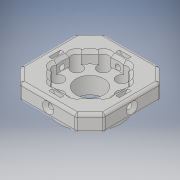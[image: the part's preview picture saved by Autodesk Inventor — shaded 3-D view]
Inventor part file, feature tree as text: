
AUTODESK INVENTOR PART (.ipt)
format: ipt  version: 2019 (Build 230136000, 136)  size: 383,488 bytes
history: native  units: in
note: dims shown in document units (in); Inventor stores cm internally (conversion verified against a paired STEP export)
features: extrude x9, sketch x6, plane x3, pattern_circular x3, chamfer x2, other x1
ambient origin geometry x8: Origin, YZ Plane, XZ Plane, XY Plane, X Axis, Y Axis, Z Axis, Center Point
bodies: Solid1 (feature_tree), Solid2 (feature_tree)
feature tree (24):
  extrude  "Extrusion1"  Depth=0.1575in TaperAngle=0.0deg
  plane  "Work Plane1"
  extrude  "Extrusion3"  Depth=1.1811in
  chamfer  "Chamfer3"  Distance=0.2362in
  sketch  "Sketch5"  dims[d23=0.6876in d24=22.5deg]
  extrude  "Extrusion6"  Depth=0.0394in
  plane  "Work Plane2"
  sketch  "Sketch4"  dims[d21=0.0787in d22=0.0394in]
  extrude  "Extrusion4"  TaperAngle=22.5deg  [1 undecoded]
  extrude  "Extrusion5"  Depth=0.1575in
  pattern_circular  "Circular Pattern1"  [2 undecoded]
  other  "Rule Fillet1"
  plane  "Work Plane4"
  sketch  "Sketch6"  dims[d25=0.1083in d26=0.1575in]
  extrude  "Extrusion7"  Depth=0.1969in TaperAngle=0.0deg
  extrude  "Extrusion8"  Depth=0.1969in TaperAngle=0.0deg
  pattern_circular  "Circular Pattern2"  Count=4 Angle=360.0deg
  chamfer  "Chamfer2"  Distance=0.0394in
  extrude  "Extrusion9"  Depth=0.315in TaperAngle=0.0deg
  extrude  "Extrusion10"  Depth=0.315in
  pattern_circular  "Circular Pattern3"  [2 undecoded]
  sketch  "Sketch1"  dims[d0=0.8661in d1=0.1575in d2=0.0in]
  sketch  "Sketch3"  dims[d17=1.1811in d18=1.1811in d19=0.2362in d20=0.0in]
  sketch  "Sketch7"  dims[d27=0.1083in d28=0.1575in d29=0.1969in d30=0.0in d31=0.1969in d32=0.0in d33=1.5748in d34=360.0deg d36=0.0394in d37=0.1575in d38=0.0in d39=0.0394in d41=0.1673in d42=0.1673in d43=0.0492in d44=0.0in d45=0.0787in d46=0.2362in d47=0.0in d48=0.0394in d49=0.0787in d50=45.0deg d51=45.0deg d52=0.0394in d53=0.0787in d54=1.5748in d55=360.0deg d57=0.3937in d58=0.2362in d59=0.0in d60=0.1969in d61=0.0787in d62=45.0deg d63=0.315in d64=45.0deg d65=0.0787in d66=0.0787in d67=0.0in d68=1.5748in d69=360.0deg d71=-0.1181in]
note: 5 required parameter values undecoded (feature->parameter linkage not recoverable at this tier; creation-order binding heuristic only, values carry confidence <= 0.55)
